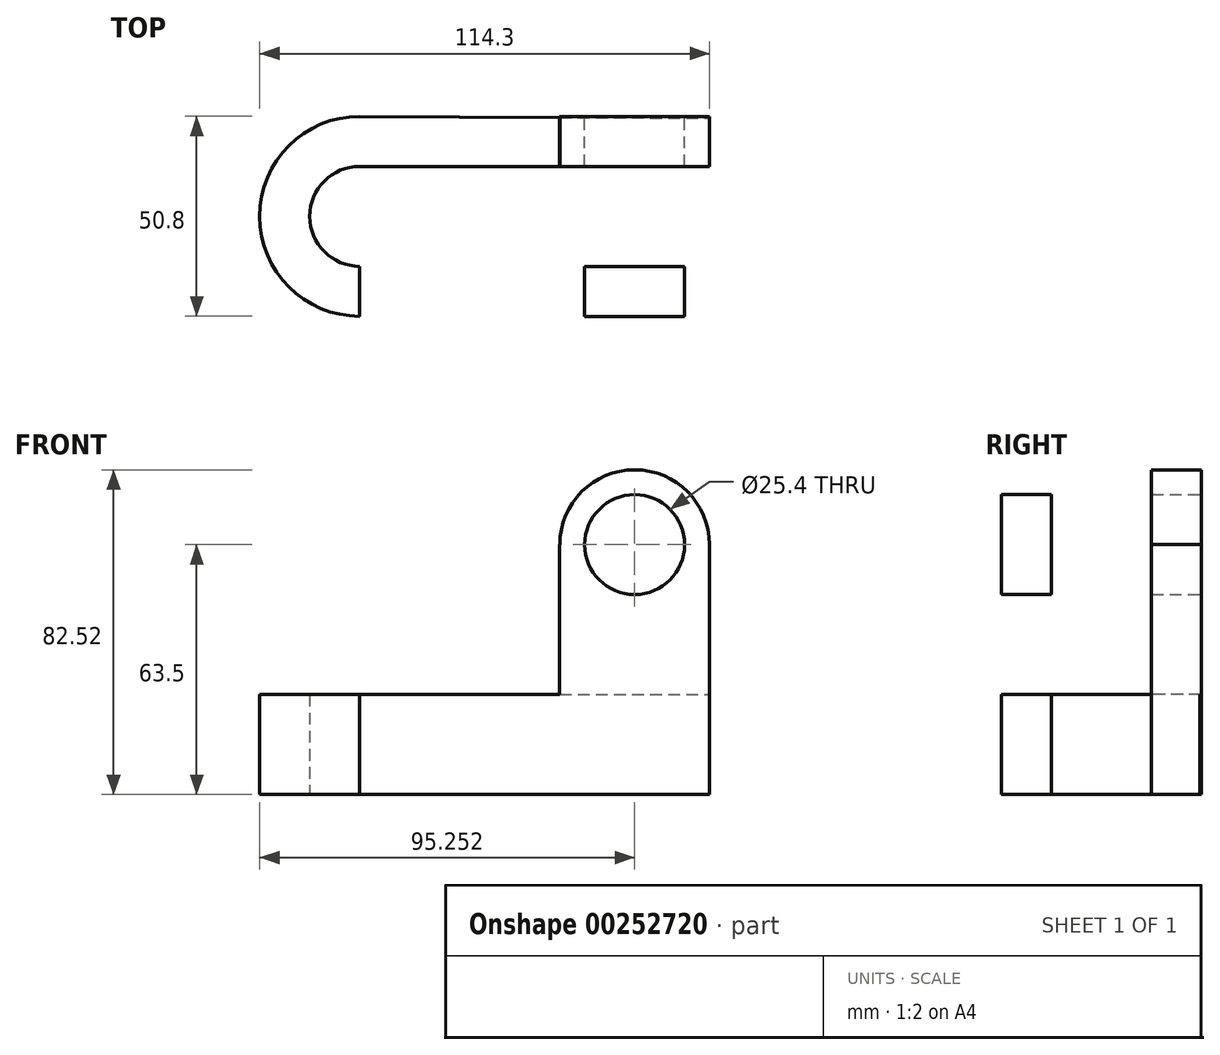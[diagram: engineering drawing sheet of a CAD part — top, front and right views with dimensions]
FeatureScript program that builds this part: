
annotation { "Feature Type Name" : "Feature", "Feature Type Description" : "" }
export const myFeature = defineFeature(function(context is Context, id is Id, definition is map)
    precondition{}
    {
        {
            var Q0;
            Q0=qCreatedBy(makeId("Top.planeOp"),FACE);
            var sketch = newSketch(context, id + "F0", { "sketchPlane" : qUnion([Q0])});
            skLineSegment(sketch, "E0", {"start": v(-65.6, 36.92) * mm, "end": v(-65.6, -13.88) * mm});
            skLineSegment(sketch, "E1", {"start": v(-65.6, -13.88) * mm, "end": v(23.3, -13.88) * mm});
            skLineSegment(sketch, "E2", {"start": v(23.3, -13.88) * mm, "end": v(23.3, 36.45) * mm});
            skLineSegment(sketch, "E3", {"start": v(-65.6, 36.92) * mm, "end": v(23.3, 36.45) * mm});
            skArc(sketch, "E4", {"start": v(-65.6, 36.92) * mm, "mid": v(-91, 11.52) * mm, "end": v(-65.6, -13.88) * mm});
            skCircle(sketch, "E5", {"center": v(-65.6, 11.52) * mm, "radius": 12.7 * mm});
            skSolve(sketch);
        }
        {
            var Q0;
            Q0 = qSketchRegion(id + "F0", true);
            extrude(context, id + "F1", {"entities" : qUnion([Q0]), "depth" : 25.4 * mm});
        }
        {
            var Q0;
            Q0=makeQuery(id+"F1.opExtrude","CAP_FACE",FACE,{"disambiguationData":[OSD([sQuery(id+"F0.wireOp",EDGE,"E1"),sQuery(id+"F0.wireOp",EDGE,"E2"),sQuery(id+"F0.wireOp",EDGE,"E3"),sQuery(id+"F0.wireOp",EDGE,"E4"),sQuery(id+"F0.wireOp",EDGE,"E5")])],"isStart":false});
            var sketch = newSketch(context, id + "F2", { "sketchPlane" : qUnion([Q0])});
            skLineSegment(sketch, "E6", {"start": v(-91, 11.52) * mm, "end": v(23.3, 11.52) * mm, "construction": true});
            skLineSegment(sketch, "E7", {"start": v(-14.8, -13.88) * mm, "end": v(-14.8, -1.18) * mm});
            skLineSegment(sketch, "E8", {"start": v(-14.8, -1.18) * mm, "end": v(23.3, -1.18) * mm});
            skLineSegment(sketch, "E9.MirrorCS", {"start": v(-14.8, 24.22) * mm, "end": v(23.3, 24.22) * mm});
            skLineSegment(sketch, "E10.MirrorCS", {"start": v(-14.8, 36.92) * mm, "end": v(-14.8, 24.22) * mm});
            skLineSegment(sketch, "E11", {"start": v(-14.8, -13.88) * mm, "end": v(23.3, -13.88) * mm});
            skLineSegment(sketch, "E12", {"start": v(23.3, -13.88) * mm, "end": v(23.3, -1.18) * mm});
            skLineSegment(sketch, "E13.MirrorCS", {"start": v(-14.8, 36.92) * mm, "end": v(23.3, 36.92) * mm});
            skLineSegment(sketch, "E14.MirrorCS", {"start": v(23.3, 36.92) * mm, "end": v(23.3, 24.22) * mm});
            skSolve(sketch);
        }
        {
            var Q0;
            {var subQ0=sQuery(id+"F2.wireOp",EDGE,"E13.MirrorCS");Q0=makeQuery(id+"F2.imprint","IMPRINT",FACE,{"disambiguationData":[TD([[makeQuery(id+"F2.imprint","IMPRINT",EDGE,{"derivedFrom":subQ0}),-1.0]])]});}
            var Q1;
            {var subQ0=sQuery(id+"F2.wireOp",EDGE,"E9.MirrorCS");Q1=makeQuery(id+"F2.imprint","IMPRINT",FACE,{"disambiguationData":[TD([[makeQuery(id+"F2.imprint","IMPRINT",EDGE,{"derivedFrom":subQ0}),1.0]])]});}
            extrude(context, id + "F3", {"entities" : qUnion([Q0, Q1]), "operationType" : NewBodyOperationType.ADD, "depth" : 38.1 * mm});
        }
        {
            var Q0;
            Q0=makeQuery(id+"F2.imprint","IMPRINT",FACE,{"disambiguationData":[TD([[makeQuery(id+"F2.imprint","IMPRINT",EDGE,{"derivedFrom":sQuery(id+"F2.wireOp",EDGE,"E7")}),-1.0]])]});
            extrude(context, id + "F4", {"entities" : qUnion([Q0]), "operationType" : NewBodyOperationType.ADD, "depth" : 38.1 * mm});
        }
        {
            var Q0;
            Q0=makeQuery(id+"F3.opExtrude","SWEPT_FACE",FACE,{"disambiguationData":[OSD([sQuery(id+"F2.wireOp",EDGE,"E13.MirrorCS")])]});
            var sketch = newSketch(context, id + "F5", { "sketchPlane" : qUnion([Q0])});
            skArc(sketch, "E15", {"start": v(14.78, 63.5) * mm, "mid": v(-4.24, 82.52) * mm, "end": v(-23.26, 63.5) * mm});
            skLineSegment(sketch, "E16.0", {"start": v(14.8, 63.5) * mm, "end": v(-23.3, 63.5) * mm});
            skSolve(sketch);
        }
        {
            var Q0;
            {var subQ0=sQuery(id+"F5.wireOp",EDGE,"E15");Q0=makeQuery(id+"F5.imprint","IMPRINT",FACE,{"disambiguationData":[TD([[makeQuery(id+"F5.imprint","IMPRINT",EDGE,{"derivedFrom":subQ0}),1.0]])]});}
            extrude(context, id + "F6", {"entities" : qUnion([Q0]), "operationType" : NewBodyOperationType.ADD, "oppositeDirection" : true, "depth" : 12.7 * mm});
        }
        {
            var Q0;
            {var subQ0=sQuery(id+"F5.wireOp",EDGE,"E15");Q0=makeQuery(id+"F5.imprint","IMPRINT",FACE,{"disambiguationData":[TD([[makeQuery(id+"F5.imprint","IMPRINT",EDGE,{"derivedFrom":subQ0}),1.0]])]});}
            var sketch = newSketch(context, id + "F7", { "sketchPlane" : qUnion([Q0])});
            skLineSegment(sketch, "E17.0", {"start": v(14.8, 63.5) * mm, "end": v(14.78, 63.5) * mm});
            skArc(sketch, "E18.0", {"start": v(14.78, 63.5) * mm, "mid": v(-4.24, 82.52) * mm, "end": v(-23.26, 63.5) * mm});
            skCircle(sketch, "E19", {"center": v(-4.24, 63.5) * mm, "radius": 12.7 * mm});
            skLineSegment(sketch, "E20.trimOffspring", {"start": v(-23.26, 63.5) * mm, "end": v(-23.3, 63.5) * mm});
            skSolve(sketch);
        }
        {
            var Q0;
            Q0 = qSketchRegion(id + "F7", true);
            extrude(context, id + "F8", {"entities" : qUnion([Q0]), "operationType" : NewBodyOperationType.REMOVE, "oppositeDirection" : true, "depth" : 38.1 * mm});
        }
        {
            var Q0;
            Q0=makeQuery(id+"F4.boolean.opBoolean","MERGE",FACE,{"derivedFrom":[makeQuery(id+"F1.opExtrude","SWEPT_FACE",FACE,{"disambiguationData":[OSD([sQuery(id+"F0.wireOp",EDGE,"E1")])]}),makeQuery(id+"F4.opExtrude","SWEPT_FACE",FACE,{"disambiguationData":[OSD([sQuery(id+"F2.wireOp",EDGE,"E11")])]})]});
            var sketch = newSketch(context, id + "F9", { "sketchPlane" : qUnion([Q0])});
            skArc(sketch, "E21", {"start": v(23.3, 63.5) * mm, "mid": v(4.24, 82.55) * mm, "end": v(-14.8, 63.5) * mm});
            skLineSegment(sketch, "E22.0", {"start": v(-14.8, 63.5) * mm, "end": v(23.3, 63.5) * mm});
            skSolve(sketch);
        }
        {
            var Q0;
            Q0=makeQuery(id+"F9.imprint","IMPRINT",FACE,{"disambiguationData":[TD([[makeQuery(id+"F9.imprint","IMPRINT",EDGE,{"derivedFrom":sQuery(id+"F9.wireOp",EDGE,"E21")}),1.0]])]});
            extrude(context, id + "F10", {"entities" : qUnion([Q0]), "operationType" : NewBodyOperationType.ADD, "oppositeDirection" : true, "depth" : 12.7 * mm});
        }
        {
            var Q0;
            Q0=makeQuery(id+"F10.boolean.opBoolean","MERGE",FACE,{"derivedFrom":[makeQuery(id+"F4.boolean.opBoolean","MERGE",FACE,{"derivedFrom":[makeQuery(id+"F1.opExtrude","SWEPT_FACE",FACE,{"disambiguationData":[OSD([sQuery(id+"F0.wireOp",EDGE,"E1")])]}),makeQuery(id+"F4.opExtrude","SWEPT_FACE",FACE,{"disambiguationData":[OSD([sQuery(id+"F2.wireOp",EDGE,"E11")])]})]}),makeQuery(id+"F10.opExtrude","CAP_FACE",FACE,{"disambiguationData":[OSD([sQuery(id+"F9.wireOp",EDGE,"E21"),sQuery(id+"F9.wireOp",EDGE,"E22.0")])],"isStart":true})]});
            var sketch = newSketch(context, id + "F11", { "sketchPlane" : qUnion([Q0])});
            skLineSegment(sketch, "E23.0", {"start": v(-14.8, 63.5) * mm, "end": v(23.3, 63.5) * mm});
            skCircle(sketch, "E24", {"center": v(4.24, 63.5) * mm, "radius": 12.7 * mm});
            skSolve(sketch);
        }
        {
            var Q0;
            {var subQ0=sQuery(id+"F11.wireOp",EDGE,"E24");var subQ1=sQuery(id+"F11.wireOp",EDGE,"E23.0");var subQ2=makeQuery(id+"F11.imprint","INTERSECT",VERTEX,{"disambiguationData":[OD(0.0)],"derivedFrom":[subQ1,subQ0]});Q0=makeQuery(id+"F11.imprint","IMPRINT",FACE,{"disambiguationData":[TD([[makeQuery(id+"F11.imprint","IMPRINT",EDGE,{"disambiguationData":[TD([[subQ2,-1.0]])],"derivedFrom":subQ1}),-1.0]])]});}
            var Q1;
            {var subQ0=sQuery(id+"F11.wireOp",EDGE,"E24");var subQ1=sQuery(id+"F11.wireOp",EDGE,"E23.0");var subQ2=makeQuery(id+"F11.imprint","INTERSECT",VERTEX,{"disambiguationData":[OD(0.0)],"derivedFrom":[subQ1,subQ0]});Q1=makeQuery(id+"F11.imprint","IMPRINT",FACE,{"disambiguationData":[TD([[makeQuery(id+"F11.imprint","IMPRINT",EDGE,{"disambiguationData":[TD([[subQ2,-1.0]])],"derivedFrom":subQ1}),1.0]])]});}
            extrude(context, id + "F12", {"entities" : qUnion([Q0, Q1]), "operationType" : NewBodyOperationType.REMOVE, "oppositeDirection" : true, "depth" : 38.1 * mm});
        }
    });
